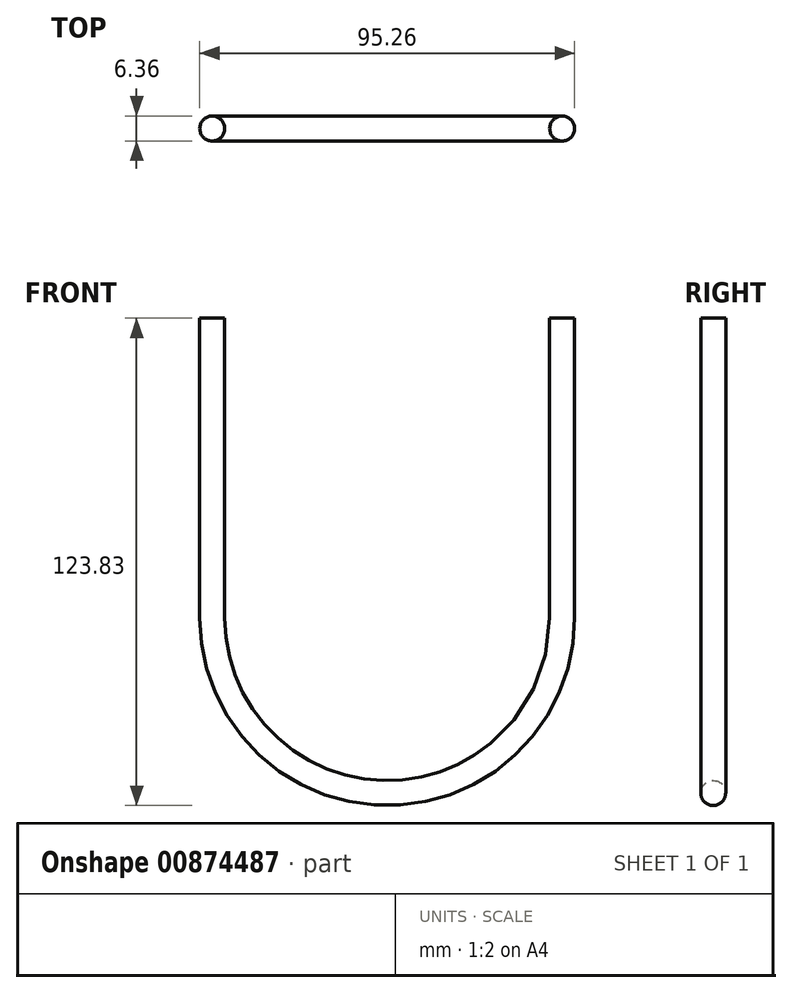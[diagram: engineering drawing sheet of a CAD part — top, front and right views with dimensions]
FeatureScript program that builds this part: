
annotation { "Feature Type Name" : "Feature", "Feature Type Description" : "" }
export const myFeature = defineFeature(function(context is Context, id is Id, definition is map)
    precondition{}
    {
        {
            var Q0;
            Q0=qCreatedBy(makeId("Front.planeOp"),FACE);
            var sketch = newSketch(context, id + "F0", { "sketchPlane" : qUnion([Q0])});
            skLineSegment(sketch, "E0", {"start": v(-44.45, 0) * mm, "end": v(-44.45, -76.2) * mm});
            skLineSegment(sketch, "E1.MirrorCS", {"start": v(44.45, 0) * mm, "end": v(44.45, -76.2) * mm});
            skArc(sketch, "E2", {"start": v(-44.45, -76.2) * mm, "mid": v(0, -120.65) * mm, "end": v(44.45, -76.2) * mm});
            skSolve(sketch);
        }
        {
            var Q0;
            Q0=qCreatedBy(makeId("Top.planeOp"),FACE);
            var sketch = newSketch(context, id + "F1", { "sketchPlane" : qUnion([Q0])});
            skCircle(sketch, "E3", {"center": v(44.45, 0) * mm, "radius": 3.17 * mm});
            skSolve(sketch);
        }
        {
            var Q0;
            Q0=makeQuery(id+"F1.imprint","IMPRINT",FACE,{"disambiguationData":[TD([[makeQuery(id+"F1.imprint","IMPRINT",EDGE,{"derivedFrom":sQuery(id+"F1.wireOp",EDGE,"E3")}),1.0]])]});
            var Q1;
            Q1 = qConstructionFilter(qBodyType(qCreatedBy(id + "F0" ,EDGE), BodyType.WIRE), ConstructionObject.NO);
            sweep(context, id + "F2", {"profiles" : qUnion([Q0]), "path" : qUnion([Q1])});
        }
    });
